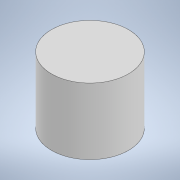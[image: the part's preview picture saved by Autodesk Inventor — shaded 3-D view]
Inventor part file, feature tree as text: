
AUTODESK INVENTOR PART (.ipt)
format: ipt  version: 2020 (Build 240168000, 168)  size: 88,064 bytes
history: native  units: mm
features: extrude x1, sketch x1
ambient origin geometry x8: Origin, YZ Plane, XZ Plane, XY Plane, X Axis, Y Axis, Z Axis, Center Point
bodies: Solid1 (feature_tree)
feature tree (2):
  extrude  "Extrusion1"  Depth=5.0mm TaperAngle=0.0deg
  sketch  "Sketch1"  dims[d0=5.8mm d1=5.0mm d2=0.0mm]
